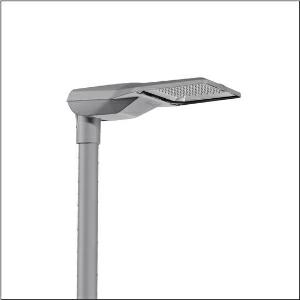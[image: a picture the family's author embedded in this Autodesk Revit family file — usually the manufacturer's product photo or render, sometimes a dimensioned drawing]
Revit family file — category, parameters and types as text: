
# Revit family: streetlight_sl_21_iq_midi___pl52_5xe3h41g08mb_9f92
name_source: partatom
category: Lighting Fixtures
units: mm (PartAtom-declared; Revit-internal decimal feet)

## family parameters
Cut with Voids When Loaded = No
Host = Face
Light Source = No
Part Type = Normal
Room Calculation Point = No
Round Connector Dimension = Use Diameter
Shared = No

## types (1)
- --- (1 x LED, 20000 lm, 146.7 W, 4000K)
    Apparent Load = 147 VA
    CIE Flux Codes = 27 59 98 100 100
    Color Rendering = 70
    Color Temperature = 4000K
    Default Elevation = 1800 mm
    Description = Streetlight SL 21 iQ midi, mast luminaire, primary light control with lens, of PMMA, primary optical cover: cover, of toughened safety glass, transparent, light distribution: PL52, light emission: direct distribution, primary light characteristic: asymmetric, installation type: post-top, side-entry, LED, High Power LED, rated luminous flux: 20.000lm, luminous efficacy: 136lm/W, light colour: 740, colour temperature: 4000K, control: Street-Remote, Auto-Match, Temp-Guard, Lumen-Switch, Night-Set, Smart-Wire, Light-Fading, Desk-Remote (wireless, voltage-free reading and setting of iQ features in the workshop via application-optimized NFC function/RFID function), optimised constant luminous flux control (CLO 2.0), presetting dimming linear, mains connection: 230..240V, AC, 50/60Hz, start of lifetime: 147W, end of service life: 161W, reduction: 62W, luminaire housing, of diecast aluminium, powder-coated, Siteco® metallic grey (DB 702S), corrosivity category C5 mid according to DIN EN ISO 12944, please order mast flange separately, inclination adjustable: 0°, 5°, 10°, 15°, sealing non-destructively replaceable, multi-level sealing system, length: 644mm, width: 335mm, height: 110mm, mast flange for spigot size: 42mm (side-entry): 5XC10008XM4, 60/48mm (side-entry/post-top): 5XC10108XM2, 76/60mm (side-entry/post-top): 5XC10108XM1, protection rating (complete): IP66, insulation class (complete): insulation class II (safety insulation), certification: CE, ENEC, ENEC+, VDE, impact resistance: IK09, permissible operating ambient temperature for outdoor applications: -40..+50°C, standard-compliant lighting for roads and squares, packaging unit: 1 piece

Light Distribution: PL52
    Height = 111 mm
    Lamp = 1 x LED
    Lamp Light Flux = 20000 lm
    Lamp Power = 146.7 W
    Lamp count = 1
    Length = 644 mm
    Luminous efficacy = 136 lm/W
    Manufacturer = Siteco
    ModVariant = No
    Model = 5XE3H41G08MB
    Number of Poles = 1
    OnlyDefault = Yes
    Power Factor = 1
    Product Name = Streetlight SL 21 iQ midi | PL52
    Product group = mast luminaire | pylon top
    ProductGroupID = 6100
    Protection Class = Protection class II
    Protection Degree = IP 66
    RLX_Detail_Level = 1
    RLX_Emergency_Light_Flux = 0 lm
    RLX_Emergency_Type = 0
    RLX_Emergency_Type_DB = No
    RlxData = <blob elided: 100345 chars, md5=82d41334>
    Socket = socket
    Standby Power = 0 W
    System Light Flux = 20000 lm
    System Power = 147 W
    Type Comments = factory setting: luminous flux: 100 % | dim-lin: 254 | 753 mA
    Type Image = l_1004298.jpg
    URL = http://relux.com
    VarID = @adj_143179
    Voltage = 0 V
    Weight = 0.00 kg
    Width = 336 mm

## geometry (parser evidence)
native form markers: Blend x4, Sweep x10
no freeform markers — native parametric forms only
